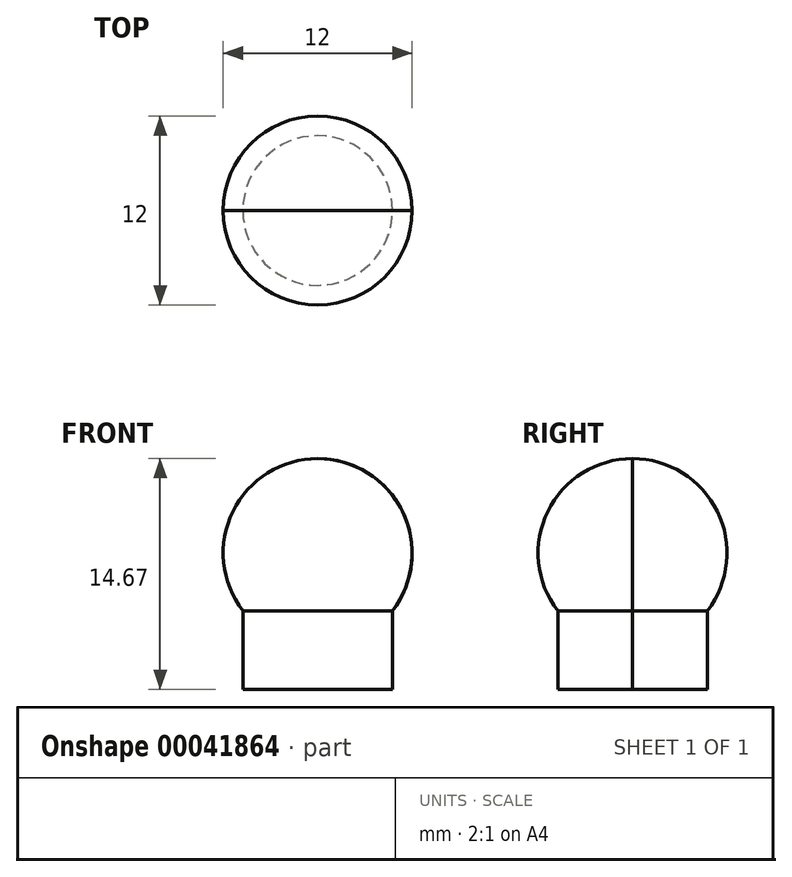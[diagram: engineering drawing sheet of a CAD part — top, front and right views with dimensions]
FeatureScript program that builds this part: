
annotation { "Feature Type Name" : "Feature", "Feature Type Description" : "" }
export const myFeature = defineFeature(function(context is Context, id is Id, definition is map)
    precondition{}
    {
        {
            var Q0;
            Q0=qCreatedBy(makeId("Front.planeOp"),FACE);
            var sketch = newSketch(context, id + "F0", { "sketchPlane" : qUnion([Q0])});
            skLineSegment(sketch, "E0.bottom", {"start": v(0, 0) * mm, "end": v(4.75, 0) * mm});
            skLineSegment(sketch, "E0.right", {"start": v(4.75, 0) * mm, "end": v(4.75, 5) * mm});
            skArc(sketch, "E1", {"start": v(4.75, 5) * mm, "mid": v(5.38, 11.31) * mm, "end": v(0, 14.67) * mm});
            skLineSegment(sketch, "E2", {"start": v(0, 0) * mm, "end": v(0, 14.67) * mm});
            skArc(sketch, "E3.MirrorCS", {"start": v(-4.75, 5) * mm, "mid": v(-5.38, 11.31) * mm, "end": v(0, 14.67) * mm, "construction": true});
            skLineSegment(sketch, "E4.MirrorCS", {"start": v(-4.75, 0) * mm, "end": v(-4.75, 5) * mm, "construction": true});
            skLineSegment(sketch, "E5.MirrorCS", {"start": v(0, 0) * mm, "end": v(-4.75, 0) * mm, "construction": true});
            skSolve(sketch);
        }
        {
            var Q0;
            Q0=makeQuery(id+"F0.imprint","IMPRINT",FACE,{"disambiguationData":[TD([[makeQuery(id+"F0.imprint","IMPRINT",EDGE,{"derivedFrom":sQuery(id+"F0.wireOp",EDGE,"E0.bottom")}),1.0]])]});
            var Q1;
            Q1=sQuery(id+"F0.wireOp",EDGE,"E2");
            revolve(context, id + "F1", {"entities" : qUnion([Q0]), "axis" : qUnion([Q1]), "revolveType" : RevolveType.FULL});
        }
        {
            var Q0;
            Q0 = qSketchRegion(id + "F0", true);
            var Q1;
            Q1=sQuery(id+"F0.wireOp",EDGE,"E2");
            revolve(context, id + "F2", {"entities" : qUnion([Q0]), "axis" : qUnion([Q1]), "revolveType" : RevolveType.TWO_DIRECTIONS, "angle" : 180 * degree, "angleBack" : 360 * degree});
        }
    });
